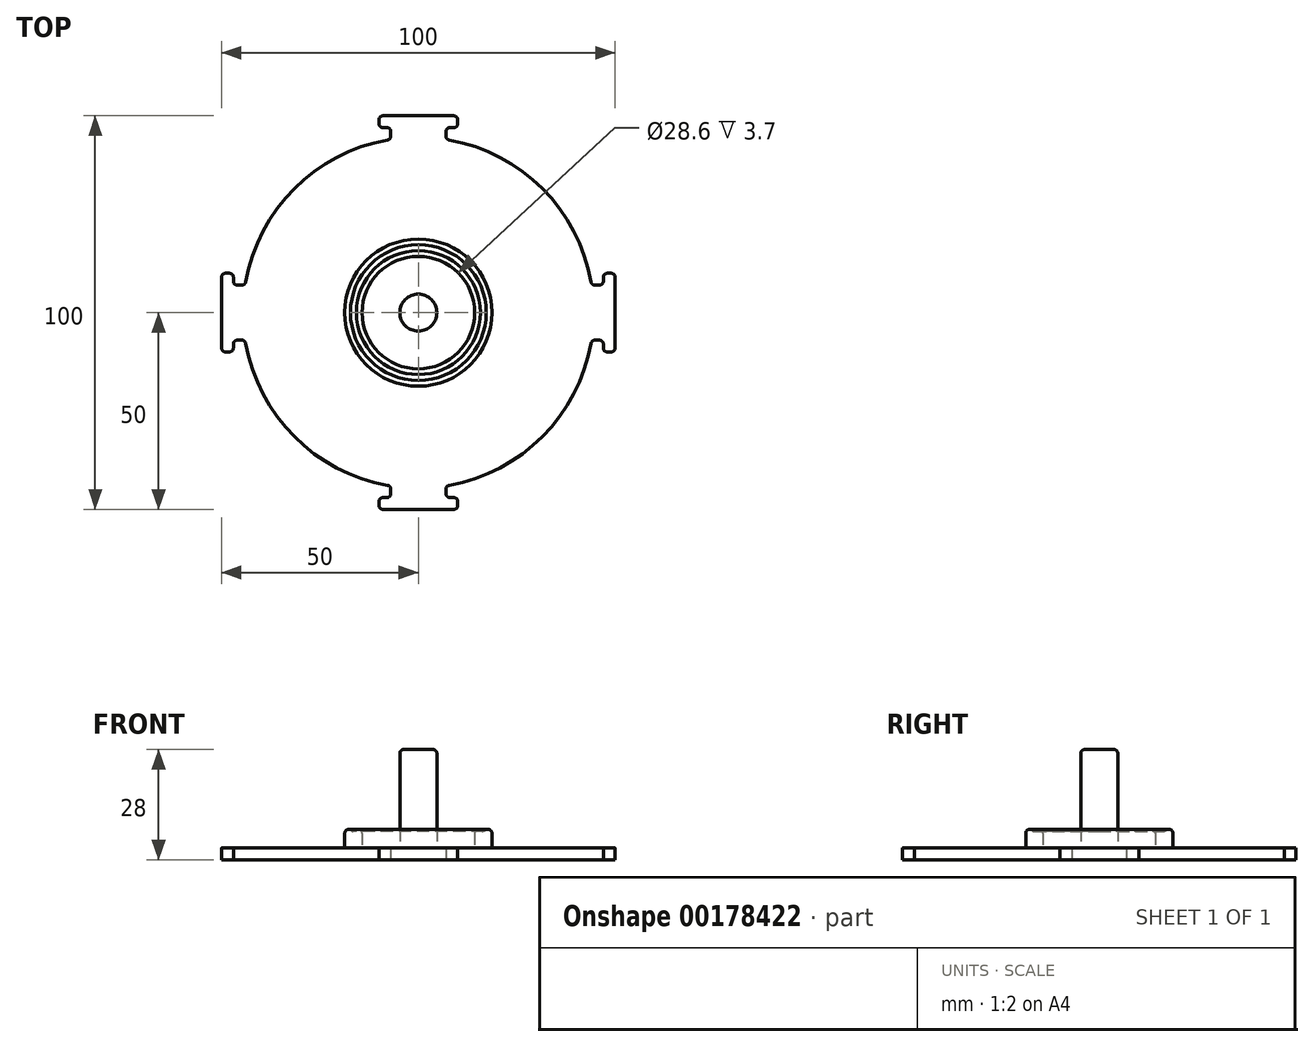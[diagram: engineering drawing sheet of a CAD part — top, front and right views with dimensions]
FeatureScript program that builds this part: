
annotation { "Feature Type Name" : "Feature", "Feature Type Description" : "" }
export const myFeature = defineFeature(function(context is Context, id is Id, definition is map)
    precondition{}
    {
        {
            var Q0;
            Q0=qCreatedBy(makeId("Top.planeOp"),FACE);
            var sketch = newSketch(context, id + "F0", { "sketchPlane" : qUnion([Q0])});
            skLineSegment(sketch, "E0", {"start": v(0, 50) * mm, "end": v(-10, 50) * mm});
            skLineSegment(sketch, "E1", {"start": v(0, 50) * mm, "end": v(0, 0) * mm});
            skLineSegment(sketch, "E2", {"start": v(-10, 50) * mm, "end": v(-10, 47) * mm});
            skLineSegment(sketch, "E3", {"start": v(-10, 47) * mm, "end": v(-7, 47) * mm});
            skLineSegment(sketch, "E4", {"start": v(-7, 47) * mm, "end": v(-7, 44) * mm});
            skArc(sketch, "E5", {"start": v(-7, 44) * mm, "mid": v(-20.24, 39.7) * mm, "end": v(-31.5, 31.5) * mm});
            skLineSegment(sketch, "E6", {"start": v(0, 0) * mm, "end": v(-31.5, 31.5) * mm});
            skSolve(sketch);
        }
        {
            var Q0;
            Q0=makeQuery(id+"F0.imprint","IMPRINT",FACE,{"disambiguationData":[TD([[makeQuery(id+"F0.imprint","IMPRINT",EDGE,{"derivedFrom":sQuery(id+"F0.wireOp",EDGE,"E0")}),1.0]])]});
            extrude(context, id + "F1", {"entities" : qUnion([Q0]), "depth" : 3 * mm});
        }
        {
            var Q0;
            Q0=makeQuery(id+"F1.opExtrude","SWEPT_EDGE",EDGE,{"disambiguationData":[OSD([sQuery(id+"F0.wireOp",EDGE,"E2"),sQuery(id+"F0.wireOp",EDGE,"E3")])]});
            var Q1;
            Q1=makeQuery(id+"F1.opExtrude","SWEPT_EDGE",EDGE,{"disambiguationData":[OSD([sQuery(id+"F0.wireOp",EDGE,"E0"),sQuery(id+"F0.wireOp",EDGE,"E2")])]});
            var Q2;
            Q2=makeQuery(id+"F1.opExtrude","SWEPT_EDGE",EDGE,{"disambiguationData":[OSD([sQuery(id+"F0.wireOp",EDGE,"E4"),sQuery(id+"F0.wireOp",EDGE,"E5")])]});
            var Q3;
            Q3=makeQuery(id+"F1.opExtrude","SWEPT_EDGE",EDGE,{"disambiguationData":[OSD([sQuery(id+"F0.wireOp",EDGE,"E3"),sQuery(id+"F0.wireOp",EDGE,"E4")])]});
            fillet(context, id + "F2", {"entities" : qUnion([Q0, Q1, Q2, Q3]), "radius" : 1 * mm, "tangentPropagation" : true, "allowEdgeOverflow" : false});
        }
        {
            var Q0;
            Q0=makeQuery(id+"F1.opExtrude","SWEPT_BODY",BODY,{"disambiguationData":[OSD([sQuery(id+"F0.wireOp",EDGE,"E0"),sQuery(id+"F0.wireOp",EDGE,"E1"),sQuery(id+"F0.wireOp",EDGE,"E2"),sQuery(id+"F0.wireOp",EDGE,"E3"),sQuery(id+"F0.wireOp",EDGE,"E4"),sQuery(id+"F0.wireOp",EDGE,"E5"),sQuery(id+"F0.wireOp",EDGE,"E6")])]});
            var Q1;
            Q1=makeQuery(id+"F1.opExtrude","SWEPT_FACE",FACE,{"disambiguationData":[OSD([sQuery(id+"F0.wireOp",EDGE,"E6")])]});
            mirror(context, id + "F3", {"operationType" : NewBodyOperationType.ADD, "entities" : qUnion([Q0]), "mirrorPlane" : qUnion([Q1])});
        }
        {
            var Q0;
            Q0=makeQuery(id+"F1.opExtrude","SWEPT_BODY",BODY,{"disambiguationData":[OSD([sQuery(id+"F0.wireOp",EDGE,"E0"),sQuery(id+"F0.wireOp",EDGE,"E1"),sQuery(id+"F0.wireOp",EDGE,"E2"),sQuery(id+"F0.wireOp",EDGE,"E3"),sQuery(id+"F0.wireOp",EDGE,"E4"),sQuery(id+"F0.wireOp",EDGE,"E5"),sQuery(id+"F0.wireOp",EDGE,"E6")])]});
            var Q1;
            {var subQ0=makeQuery(id+"F1.opExtrude","SWEPT_EDGE",EDGE,{"disambiguationData":[OSD([sQuery(id+"F0.wireOp",EDGE,"E1"),sQuery(id+"F0.wireOp",EDGE,"E6")])]});Q1=makeQuery(id+"F3.boolean.opBoolean","MERGE",EDGE,{"derivedFrom":[subQ0,makeQuery(id+"F3.opPattern","COPY",EDGE,{"derivedFrom":subQ0,"instanceName":"1"})]});}
            circularPattern(context, id + "F4", {"operationType" : NewBodyOperationType.ADD, "entities" : qUnion([Q0]), "axis" : qUnion([Q1]), "angle" : 90 * degree, "instanceCount" : 4});
        }
        {
            var Q0;
            {var subQ0=makeQuery(id+"F1.opExtrude","CAP_FACE",FACE,{"disambiguationData":[OSD([sQuery(id+"F0.wireOp",EDGE,"E0"),sQuery(id+"F0.wireOp",EDGE,"E1"),sQuery(id+"F0.wireOp",EDGE,"E2"),sQuery(id+"F0.wireOp",EDGE,"E3"),sQuery(id+"F0.wireOp",EDGE,"E4"),sQuery(id+"F0.wireOp",EDGE,"E5"),sQuery(id+"F0.wireOp",EDGE,"E6")])],"isStart":false});var subQ1=makeQuery(id+"F3.boolean.opBoolean","MERGE",FACE,{"derivedFrom":[subQ0,makeQuery(id+"F3.opPattern","COPY",FACE,{"derivedFrom":subQ0,"instanceName":"1"})]});Q0=makeQuery(id+"F4.boolean.opBoolean","MERGE",FACE,{"derivedFrom":[subQ1,makeQuery(id+"F4.opPattern","COPY",FACE,{"derivedFrom":subQ1,"instanceName":"1"}),makeQuery(id+"F4.opPattern","COPY",FACE,{"derivedFrom":subQ1,"instanceName":"2"}),makeQuery(id+"F4.opPattern","COPY",FACE,{"derivedFrom":subQ1,"instanceName":"3"})]});}
            var sketch = newSketch(context, id + "F5", { "sketchPlane" : qUnion([Q0])});
            skCircle(sketch, "E7", {"center": v(0, 0) * mm, "radius": 4.7 * mm});
            skCircle(sketch, "E8", {"center": v(0, 0) * mm, "radius": 14.3 * mm});
            skCircle(sketch, "E9", {"center": v(0, 0) * mm, "radius": 18.7 * mm});
            skLineSegment(sketch, "E10", {"start": v(-14.3, 0) * mm, "end": v(-18.7, 0) * mm});
            skSolve(sketch);
        }
        {
            var Q0;
            Q0=makeQuery(id+"F5.imprint","IMPRINT",FACE,{"disambiguationData":[TD([[makeQuery(id+"F5.imprint","IMPRINT",EDGE,{"derivedFrom":sQuery(id+"F5.wireOp",EDGE,"E8")}),-1.0]])]});
            extrude(context, id + "F6", {"entities" : qUnion([Q0]), "operationType" : NewBodyOperationType.ADD, "depth" : 4.7 * mm});
        }
        {
            var Q0;
            Q0=makeQuery(id+"F5.imprint","IMPRINT",FACE,{"disambiguationData":[TD([[makeQuery(id+"F5.imprint","IMPRINT",EDGE,{"derivedFrom":sQuery(id+"F5.wireOp",EDGE,"E7")}),1.0]])]});
            var Q1;
            Q1=sQuery(id+"F5.wireOp",EDGE,"E7");
            extrude(context, id + "F7", {"entities" : qUnion([Q0]), "operationType" : NewBodyOperationType.ADD, "surfaceEntities" : qUnion([Q1]), "depth" : 25 * mm});
        }
        {
            var Q0;
            Q0=makeQuery(id+"F6.opExtrude","CAP_EDGE",EDGE,{"disambiguationData":[OSD([sQuery(id+"F5.wireOp",EDGE,"E9")])],"isStart":false});
            var Q1;
            Q1=makeQuery(id+"F6.opExtrude","CAP_EDGE",EDGE,{"disambiguationData":[OSD([sQuery(id+"F5.wireOp",EDGE,"E8")])],"isStart":false});
            var Q2;
            Q2=makeQuery(id+"F7.opExtrude","CAP_EDGE",EDGE,{"disambiguationData":[OSD([sQuery(id+"F5.wireOp",EDGE,"E7")])],"isStart":false});
            fillet(context, id + "F8", {"entities" : qUnion([Q0, Q1, Q2]), "radius" : 1 * mm, "tangentPropagation" : true, "allowEdgeOverflow" : false});
        }
        {
            var Q0;
            Q0=makeQuery(id+"F6.opExtrude","CAP_FACE",FACE,{"disambiguationData":[OSD([sQuery(id+"F5.wireOp",EDGE,"E8"),sQuery(id+"F5.wireOp",EDGE,"E9")])],"isStart":false});
            var sketch = newSketch(context, id + "F9", { "sketchPlane" : qUnion([Q0])});
            skCircle(sketch, "E11", {"center": v(0, 0) * mm, "radius": 15.75 * mm});
            skCircle(sketch, "E12", {"center": v(0, 0) * mm, "radius": 17.25 * mm});
            skSolve(sketch);
        }
        {
            var Q0;
            Q0=makeQuery(id+"F9.imprint","IMPRINT",FACE,{"disambiguationData":[TD([[makeQuery(id+"F9.imprint","IMPRINT",EDGE,{"derivedFrom":sQuery(id+"F9.wireOp",EDGE,"E11")}),-1.0]])]});
            extrude(context, id + "F10", {"entities" : qUnion([Q0]), "operationType" : NewBodyOperationType.REMOVE, "oppositeDirection" : true, "depth" : 0.5 * mm});
        }
        {
            var Q0;
            Q0=makeQuery(id+"F10.boolean.opBoolean","COPY",EDGE,{"derivedFrom":makeQuery(id+"F10.opExtrude","CAP_EDGE",EDGE,{"disambiguationData":[OSD([sQuery(id+"F9.wireOp",EDGE,"E12")])],"isStart":false})});
            var Q1;
            Q1=makeQuery(id+"F10.boolean.opBoolean","COPY",EDGE,{"derivedFrom":makeQuery(id+"F10.opExtrude","CAP_EDGE",EDGE,{"disambiguationData":[OSD([sQuery(id+"F9.wireOp",EDGE,"E11")])],"isStart":false})});
            fillet(context, id + "F11", {"entities" : qUnion([Q0, Q1]), "radius" : 0.75 * mm, "tangentPropagation" : true, "allowEdgeOverflow" : false});
        }
    });
